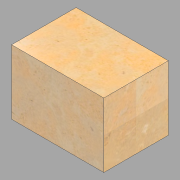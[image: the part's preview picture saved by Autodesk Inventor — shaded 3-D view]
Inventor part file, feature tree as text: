
AUTODESK INVENTOR PART (.ipt)
format: ipt  version: 2022.2 (Build 262287000, 287)  size: 131,072 bytes
history: native  units: in
note: dims shown in document units (in); Inventor stores cm internally (conversion verified against a paired STEP export)
features: extrude x1, sketch x1
ambient origin geometry x8: Origin, YZ Plane, XZ Plane, XY Plane, X Axis, Y Axis, Z Axis, Center Point
bodies: Solid1 (feature_tree)
feature tree (2):
  extrude  "Extrusion1"  Depth=3.5in
  sketch  "Sketch1"  dims[d0=3.5in d1=3.5in d2=5.0in d3=0.0in]
